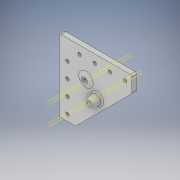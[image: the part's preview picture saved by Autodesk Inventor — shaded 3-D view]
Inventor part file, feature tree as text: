
AUTODESK INVENTOR PART (.ipt)
format: ipt  version: 2018 (Build 220112000, 112)  size: 211,968 bytes
history: native  units: in
note: dims shown in document units (in); Inventor stores cm internally (conversion verified against a paired STEP export)
features: sketch x7, extrude x5, plane x4, revolve x2, fillet x2, projected_geometry x2
ambient origin geometry x8: Origin, YZ Plane, XZ Plane, XY Plane, X Axis, Y Axis, Z Axis, Center Point
bodies: Solid1 (feature_tree)
feature tree (22):
  extrude  "Extrusion1"  Depth=0.7874in
  extrude  "Extrusion2"  Depth=3.5433in
  plane  "Work Plane2"
  revolve  "Revolution1"  [1 undecoded]
  extrude  "Extrusion3"  Depth=0.5512in
  extrude  "Extrusion4"  [1 undecoded]
  extrude  "Extrusion5"  Depth=0.0787in
  plane  "Work Plane4"
  revolve  "Revolution2"  [1 undecoded]
  fillet  "Fillet2"  Radius=0.1575in
  fillet  "Fillet3"  Radius=0.1654in
  sketch  "Sketch1"  dims[d0=0.7874in d1=0.7874in]
  sketch  "Sketch2"  dims[d2=3.5433in d3=3.5433in]
  plane  "Work Plane1"
  sketch  "Sketch3"  dims[d4=0.2362in d5=0.0in d6=0.1969in]
  sketch  "Sketch4"  dims[d7=1.2992in d8=0.5512in]
  projected_geometry  "Projected Loop1"
  sketch  "Sketch5"  dims[d9=0.2362in d10=0.0in d11=-0.0984in]
  sketch  "Sketch7"  dims[d12=0.3543in d13=0.0787in]
  plane  "Work Plane3"
  sketch  "Sketch8"  dims[d14=90.0deg d15=0.2362in d16=0.0in d17=0.1575in d18=0.1654in d19=0.315in d20=0.748in d21=0.748in d22=0.748in d23=0.315in d24=0.748in d25=0.748in d26=0.748in d27=0.2362in d28=0.0in d30=0.3543in d32=0.3543in d33=0.1969in d34=0.0in d35=0.0984in d36=0.1575in d37=0.0591in d38=0.3937in d39=90.0deg d40=0.0787in d41=0.0787in]
  projected_geometry  "Projected Loop2"
note: 3 required parameter values undecoded (feature->parameter linkage not recoverable at this tier; creation-order binding heuristic only, values carry confidence <= 0.55)